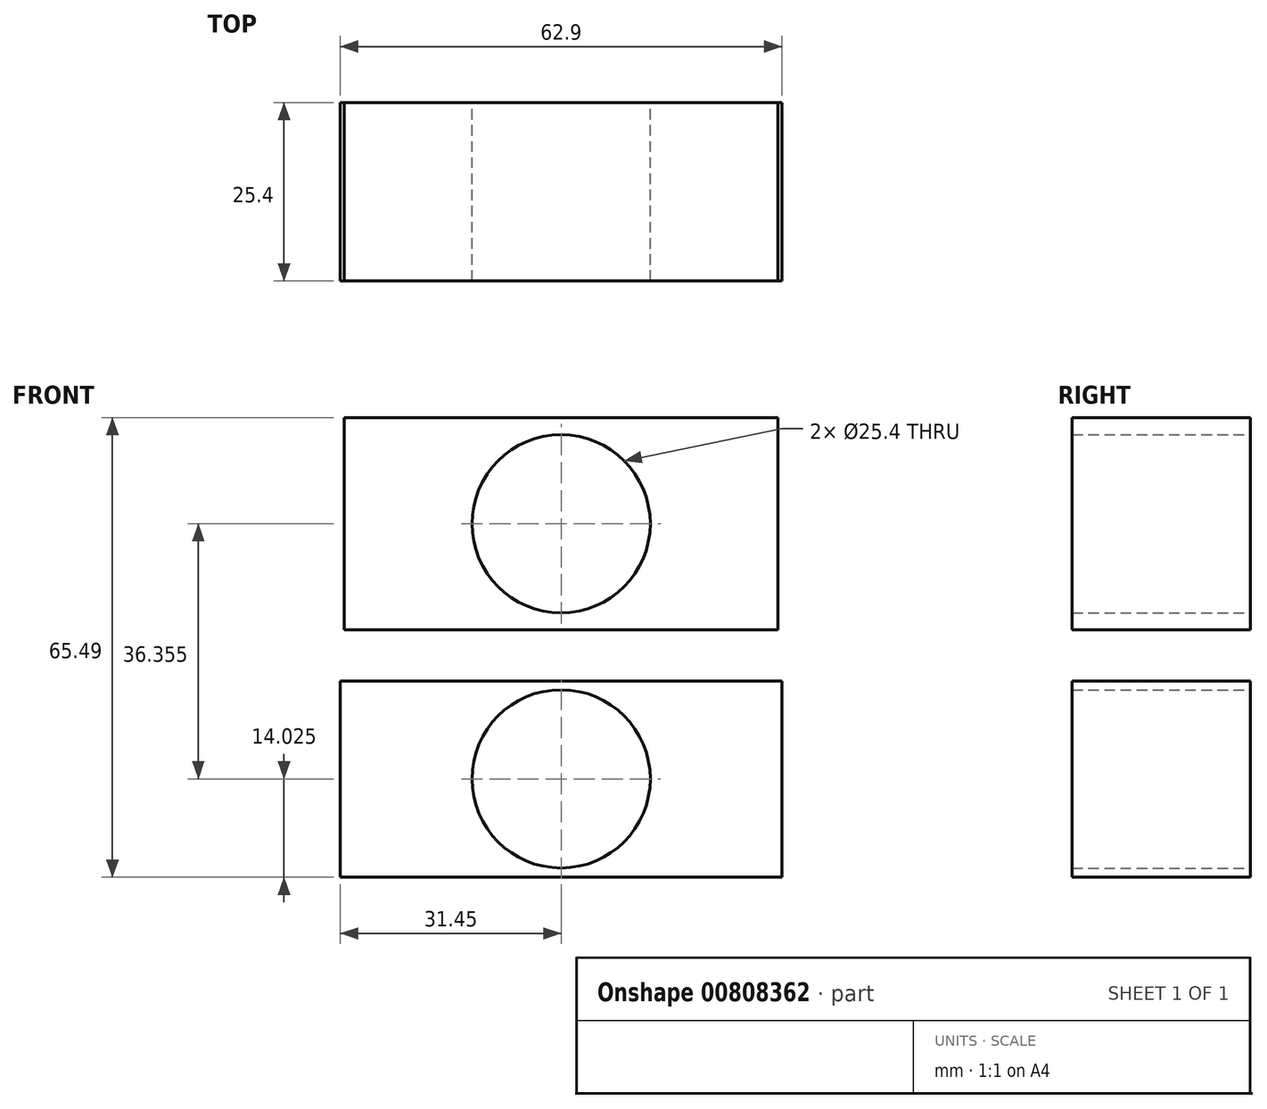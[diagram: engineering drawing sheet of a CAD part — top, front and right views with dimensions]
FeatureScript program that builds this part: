
annotation { "Feature Type Name" : "Feature", "Feature Type Description" : "" }
export const myFeature = defineFeature(function(context is Context, id is Id, definition is map)
    precondition{}
    {
        {
            var Q0;
            Q0=qCreatedBy(makeId("Front.planeOp"),FACE);
            var sketch = newSketch(context, id + "F0", { "sketchPlane" : qUnion([Q0])});
            skLineSegment(sketch, "E0.bottom", {"start": v(-31.45, -50.38) * mm, "end": v(31.45, -50.38) * mm});
            skLineSegment(sketch, "E0.top", {"start": v(-31.45, -22.39) * mm, "end": v(31.45, -22.39) * mm});
            skLineSegment(sketch, "E0.left", {"start": v(-31.45, -50.38) * mm, "end": v(-31.45, -22.39) * mm});
            skLineSegment(sketch, "E0.right", {"start": v(31.45, -50.38) * mm, "end": v(31.45, -22.39) * mm});
            skPoint(sketch, "E0.middle", {"position": v(0, -36.38) * mm});
            skLineSegment(sketch, "E1.bottom", {"start": v(-30.89, -15.1) * mm, "end": v(30.89, -15.1) * mm});
            skLineSegment(sketch, "E1.top", {"start": v(-30.89, 15.1) * mm, "end": v(30.89, 15.1) * mm});
            skLineSegment(sketch, "E1.left", {"start": v(-30.89, -15.1) * mm, "end": v(-30.89, 15.1) * mm});
            skLineSegment(sketch, "E1.right", {"start": v(30.89, -15.1) * mm, "end": v(30.89, 15.1) * mm});
            skPoint(sketch, "E1.middle", {"position": v(0, 0) * mm});
            skSolve(sketch);
        }
        {
            var Q0;
            Q0 = qSketchRegion(id + "F0", true);
            extrude(context, id + "F1", {"entities" : qUnion([Q0]), "depth" : 25.4 * mm, "offsetDistance" : 25.4 * mm});
        }
        {
            var Q0;
            Q0=qCreatedBy(makeId("Front.planeOp"),FACE);
            var sketch = newSketch(context, id + "F2", { "sketchPlane" : qUnion([Q0])});
            skCircle(sketch, "E2", {"center": v(0, 0) * mm, "radius": 12.7 * mm});
            skCircle(sketch, "E3", {"center": v(0, -36.35) * mm, "radius": 12.7 * mm});
            skSolve(sketch);
        }
        {
            var Q0;
            Q0=sQuery(id+"F2.wireOp",VERTEX,"E2.center");
            var Q1;
            Q1=sQuery(id+"F2.wireOp",VERTEX,"E3.center");
            var Q2;
            Q2=makeQuery(id+"F1.opExtrude","SWEPT_BODY",BODY,{"disambiguationData":[OSD([sQuery(id+"F0.wireOp",EDGE,"E1.bottom"),sQuery(id+"F0.wireOp",EDGE,"E1.top"),sQuery(id+"F0.wireOp",EDGE,"E1.left"),sQuery(id+"F0.wireOp",EDGE,"E1.right")])]});
            var Q3;
            Q3=makeQuery(id+"F1.opExtrude","SWEPT_BODY",BODY,{"disambiguationData":[OSD([sQuery(id+"F0.wireOp",EDGE,"E0.bottom"),sQuery(id+"F0.wireOp",EDGE,"E0.top"),sQuery(id+"F0.wireOp",EDGE,"E0.left"),sQuery(id+"F0.wireOp",EDGE,"E0.right")])]});
            hole(context, id + "F3", {"style" : HoleStyle.SIMPLE, "endStyle" : HoleEndStyle.THROUGH, "oppositeDirection" : true, "holeDiameter" : 25.4 * mm, "majorDiameter" : 6.35 * mm, "isTappedThrough" : true, "tappedDepth" : 12.7 * mm, "tapClearance" : 3, "locations" : qUnion([Q0, Q1]), "scope" : qUnion([Q2, Q3])});
        }
    });
